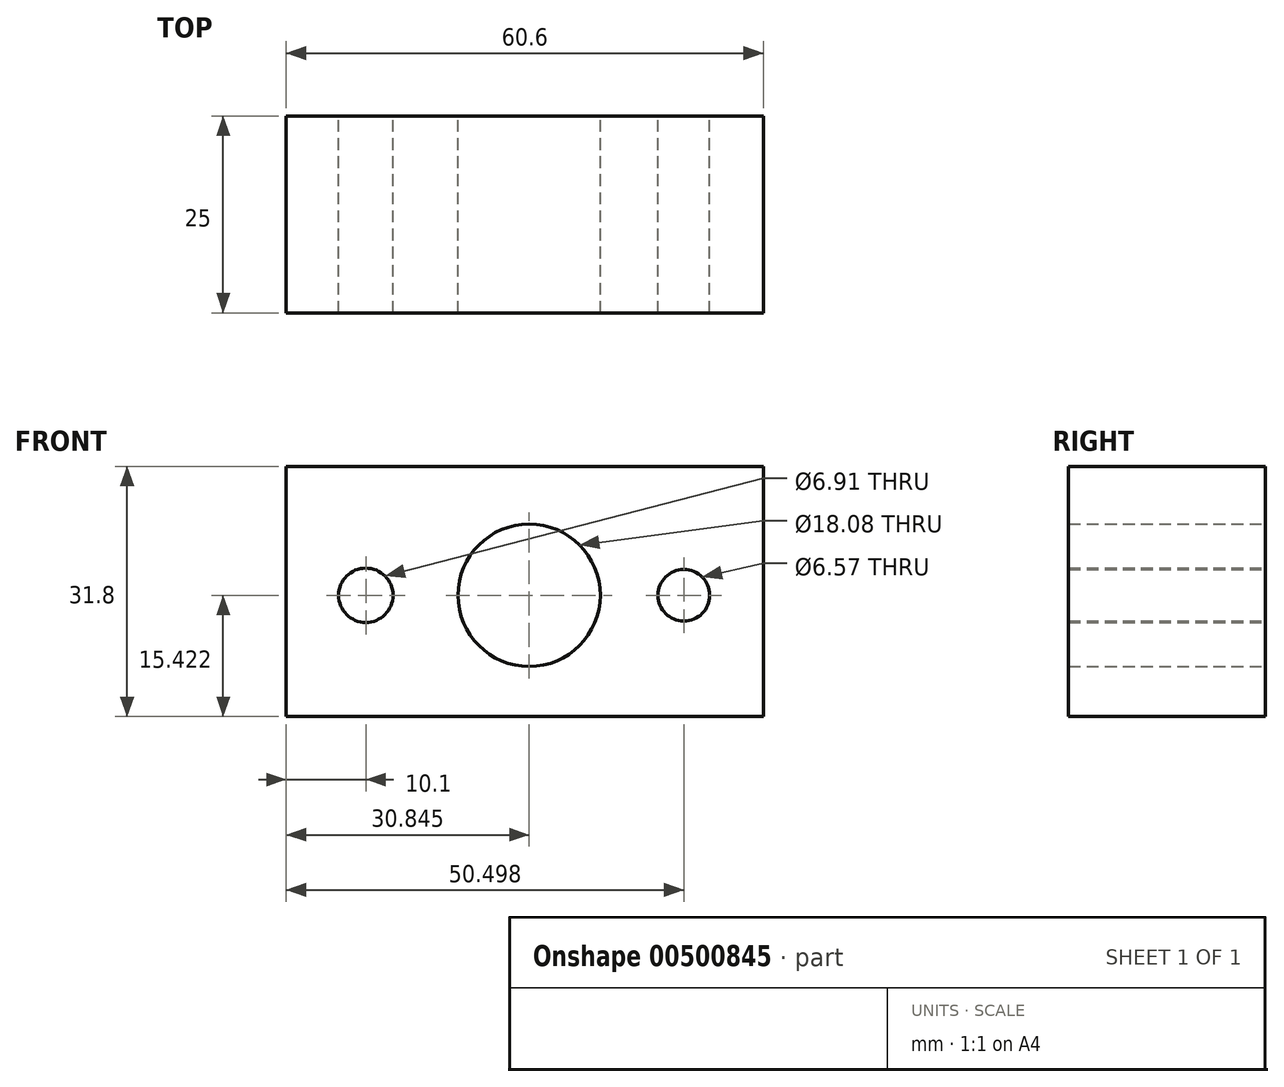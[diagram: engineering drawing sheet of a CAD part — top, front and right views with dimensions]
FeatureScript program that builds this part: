
annotation { "Feature Type Name" : "Feature", "Feature Type Description" : "" }
export const myFeature = defineFeature(function(context is Context, id is Id, definition is map)
    precondition{}
    {
        {
            var Q0;
            Q0=qCreatedBy(makeId("Front.planeOp"),FACE);
            var sketch = newSketch(context, id + "F0", { "sketchPlane" : qUnion([Q0])});
            skLineSegment(sketch, "E0.bottom", {"start": v(0, 0) * mm, "end": v(60.6, 0) * mm});
            skLineSegment(sketch, "E0.top", {"start": v(0, 31.8) * mm, "end": v(60.6, 31.8) * mm});
            skLineSegment(sketch, "E0.left", {"start": v(0, 0) * mm, "end": v(0, 31.8) * mm});
            skLineSegment(sketch, "E0.right", {"start": v(60.6, 0) * mm, "end": v(60.6, 31.8) * mm});
            skCircle(sketch, "E1", {"center": v(30.84, 15.42) * mm, "radius": 9.04 * mm});
            skCircle(sketch, "E2", {"center": v(10.1, 15.42) * mm, "radius": 3.45 * mm});
            skCircle(sketch, "E3", {"center": v(50.5, 15.42) * mm, "radius": 3.29 * mm});
            skSolve(sketch);
        }
        {
            var Q0;
            Q0 = qSketchRegion(id + "F0", true);
            extrude(context, id + "F1", {"entities" : qUnion([Q0]), "depth" : 25 * mm});
        }
    });
